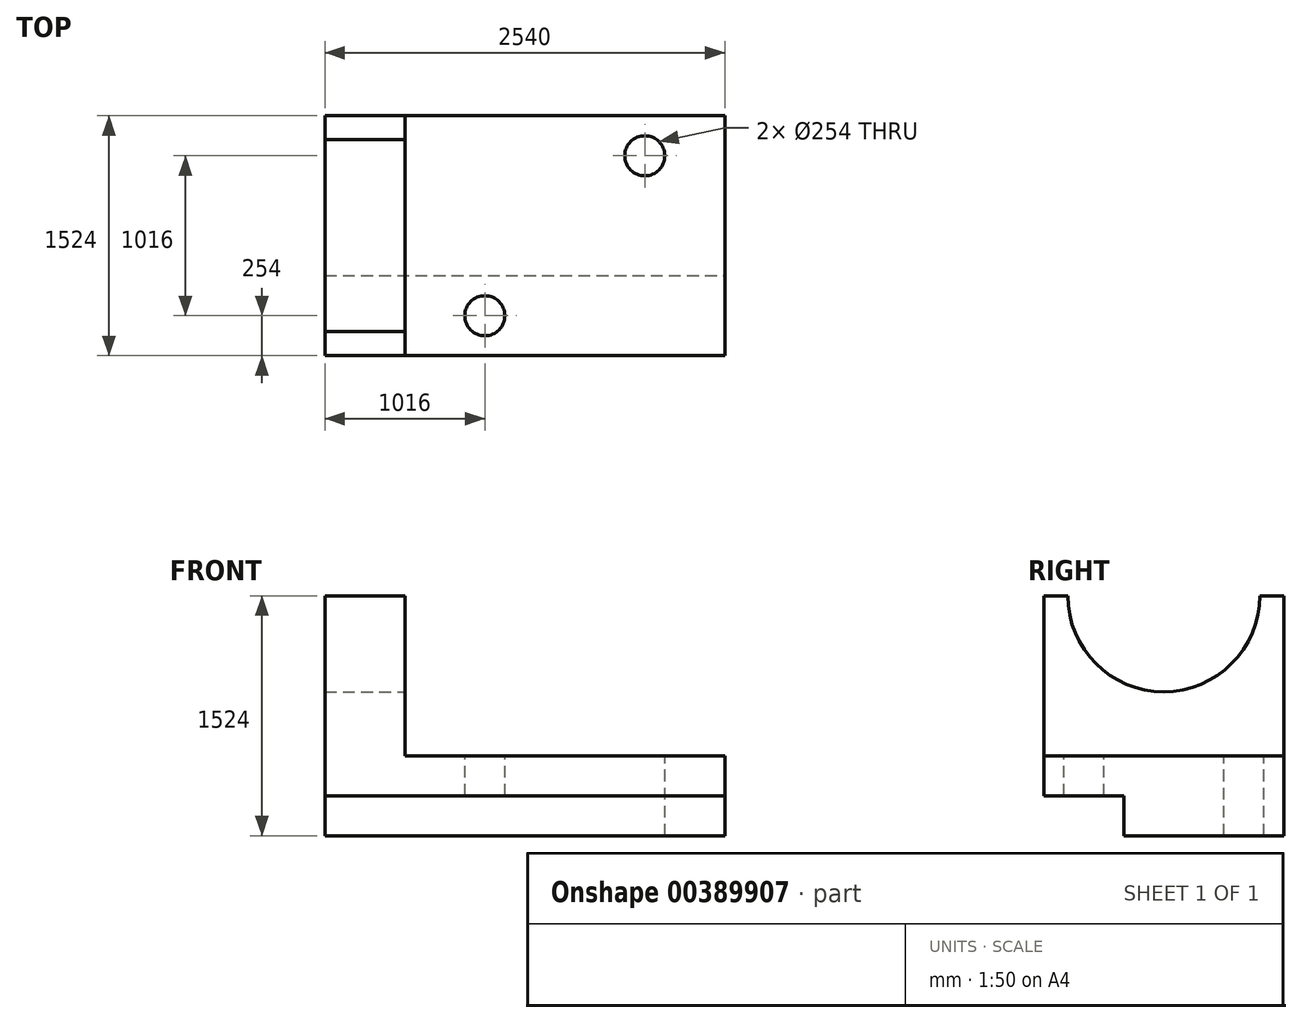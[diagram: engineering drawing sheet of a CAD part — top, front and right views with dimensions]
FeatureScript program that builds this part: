
annotation { "Feature Type Name" : "Feature", "Feature Type Description" : "" }
export const myFeature = defineFeature(function(context is Context, id is Id, definition is map)
    precondition{}
    {
        {
            var Q0;
            Q0=qCreatedBy(makeId("Front.planeOp"),FACE);
            var sketch = newSketch(context, id + "F0", { "sketchPlane" : qUnion([Q0])});
            skLineSegment(sketch, "E0.bottom", {"start": v(-1266.86, 738.3) * mm, "end": v(1273.14, 738.3) * mm});
            skLineSegment(sketch, "E0.top", {"start": v(-1266.86, -785.7) * mm, "end": v(1273.14, -785.7) * mm});
            skLineSegment(sketch, "E0.left", {"start": v(-1266.86, 738.3) * mm, "end": v(-1266.86, -785.7) * mm});
            skLineSegment(sketch, "E0.right", {"start": v(1273.14, 738.3) * mm, "end": v(1273.14, -785.7) * mm});
            skSolve(sketch);
        }
        {
            var Q0;
            Q0 = qSketchRegion(id + "F0", true);
            extrude(context, id + "F1", {"entities" : qUnion([Q0]), "depth" : 1524 * mm});
        }
        {
            var Q0;
            Q0=makeQuery(id+"F1.opExtrude","SWEPT_FACE",FACE,{"disambiguationData":[OSD([sQuery(id+"F0.wireOp",EDGE,"E0.bottom")])]});
            var sketch = newSketch(context, id + "F2", { "sketchPlane" : qUnion([Q0])});
            skLineSegment(sketch, "E1.bottom", {"start": v(-758.86, 198.1) * mm, "end": v(1741.87, 198.1) * mm});
            skLineSegment(sketch, "E1.top", {"start": v(-758.86, -1793.82) * mm, "end": v(1741.87, -1793.82) * mm});
            skLineSegment(sketch, "E1.left", {"start": v(-758.86, 198.1) * mm, "end": v(-758.86, -1793.82) * mm});
            skLineSegment(sketch, "E1.right", {"start": v(1741.87, 198.1) * mm, "end": v(1741.87, -1793.82) * mm});
            skSolve(sketch);
        }
        {
            var Q0;
            Q0 = qSketchRegion(id + "F2", true);
            extrude(context, id + "F3", {"entities" : qUnion([Q0]), "operationType" : NewBodyOperationType.REMOVE, "oppositeDirection" : true, "depth" : 1016 * mm});
        }
        {
            var Q0;
            Q0=makeQuery(id+"F1.opExtrude","SWEPT_FACE",FACE,{"disambiguationData":[OSD([sQuery(id+"F0.wireOp",EDGE,"E0.right")])]});
            var sketch = newSketch(context, id + "F4", { "sketchPlane" : qUnion([Q0])});
            skLineSegment(sketch, "E2.bottom", {"start": v(-1687.53, -531.7) * mm, "end": v(-1016, -531.7) * mm});
            skLineSegment(sketch, "E2.top", {"start": v(-1687.53, -893.3) * mm, "end": v(-1016, -893.3) * mm});
            skLineSegment(sketch, "E2.left", {"start": v(-1687.53, -531.7) * mm, "end": v(-1687.53, -893.3) * mm});
            skLineSegment(sketch, "E2.right", {"start": v(-1016, -531.7) * mm, "end": v(-1016, -893.3) * mm});
            skSolve(sketch);
        }
        {
            var Q0;
            Q0 = qSketchRegion(id + "F4", true);
            extrude(context, id + "F5", {"entities" : qUnion([Q0]), "operationType" : NewBodyOperationType.REMOVE, "endBound" : BoundingType.THROUGH_ALL, "oppositeDirection" : true, "depth" : 25.4 * mm});
        }
        {
            var Q0;
            Q0=makeQuery(id+"F3.boolean.opBoolean","COPY",FACE,{"derivedFrom":makeQuery(id+"F3.opExtrude","SWEPT_FACE",FACE,{"disambiguationData":[OSD([sQuery(id+"F2.wireOp",EDGE,"E1.left")])]})});
            var sketch = newSketch(context, id + "F6", { "sketchPlane" : qUnion([Q0])});
            skCircle(sketch, "E3", {"center": v(-762, 738.3) * mm, "radius": 609.6 * mm});
            skSolve(sketch);
        }
        {
            var Q0;
            Q0 = qSketchRegion(id + "F6", true);
            extrude(context, id + "F7", {"entities" : qUnion([Q0]), "operationType" : NewBodyOperationType.REMOVE, "endBound" : BoundingType.THROUGH_ALL, "oppositeDirection" : true, "depth" : 25.4 * mm});
        }
        {
            var Q0;
            Q0=makeQuery(id+"F3.boolean.opBoolean","COPY",FACE,{"derivedFrom":makeQuery(id+"F3.opExtrude","CAP_FACE",FACE,{"disambiguationData":[OSD([sQuery(id+"F2.wireOp",EDGE,"E1.bottom"),sQuery(id+"F2.wireOp",EDGE,"E1.top"),sQuery(id+"F2.wireOp",EDGE,"E1.left"),sQuery(id+"F2.wireOp",EDGE,"E1.right")])],"isStart":false})});
            var sketch = newSketch(context, id + "F8", { "sketchPlane" : qUnion([Q0])});
            skCircle(sketch, "E4", {"center": v(765.14, -254) * mm, "radius": 127 * mm});
            skSolve(sketch);
        }
        {
            var Q0;
            Q0 = qSketchRegion(id + "F8", true);
            extrude(context, id + "F9", {"entities" : qUnion([Q0]), "operationType" : NewBodyOperationType.REMOVE, "endBound" : BoundingType.THROUGH_ALL, "oppositeDirection" : true, "depth" : 25.4 * mm});
        }
        {
            var Q0;
            Q0=makeQuery(id+"F3.boolean.opBoolean","COPY",FACE,{"derivedFrom":makeQuery(id+"F3.opExtrude","CAP_FACE",FACE,{"disambiguationData":[OSD([sQuery(id+"F2.wireOp",EDGE,"E1.bottom"),sQuery(id+"F2.wireOp",EDGE,"E1.top"),sQuery(id+"F2.wireOp",EDGE,"E1.left"),sQuery(id+"F2.wireOp",EDGE,"E1.right")])],"isStart":false})});
            var sketch = newSketch(context, id + "F10", { "sketchPlane" : qUnion([Q0])});
            skCircle(sketch, "E5", {"center": v(-250.86, -1270) * mm, "radius": 127 * mm});
            skSolve(sketch);
        }
        {
            var Q0;
            Q0 = qSketchRegion(id + "F10", true);
            extrude(context, id + "F11", {"entities" : qUnion([Q0]), "operationType" : NewBodyOperationType.REMOVE, "endBound" : BoundingType.THROUGH_ALL, "oppositeDirection" : true, "depth" : 25.4 * mm});
        }
    });
